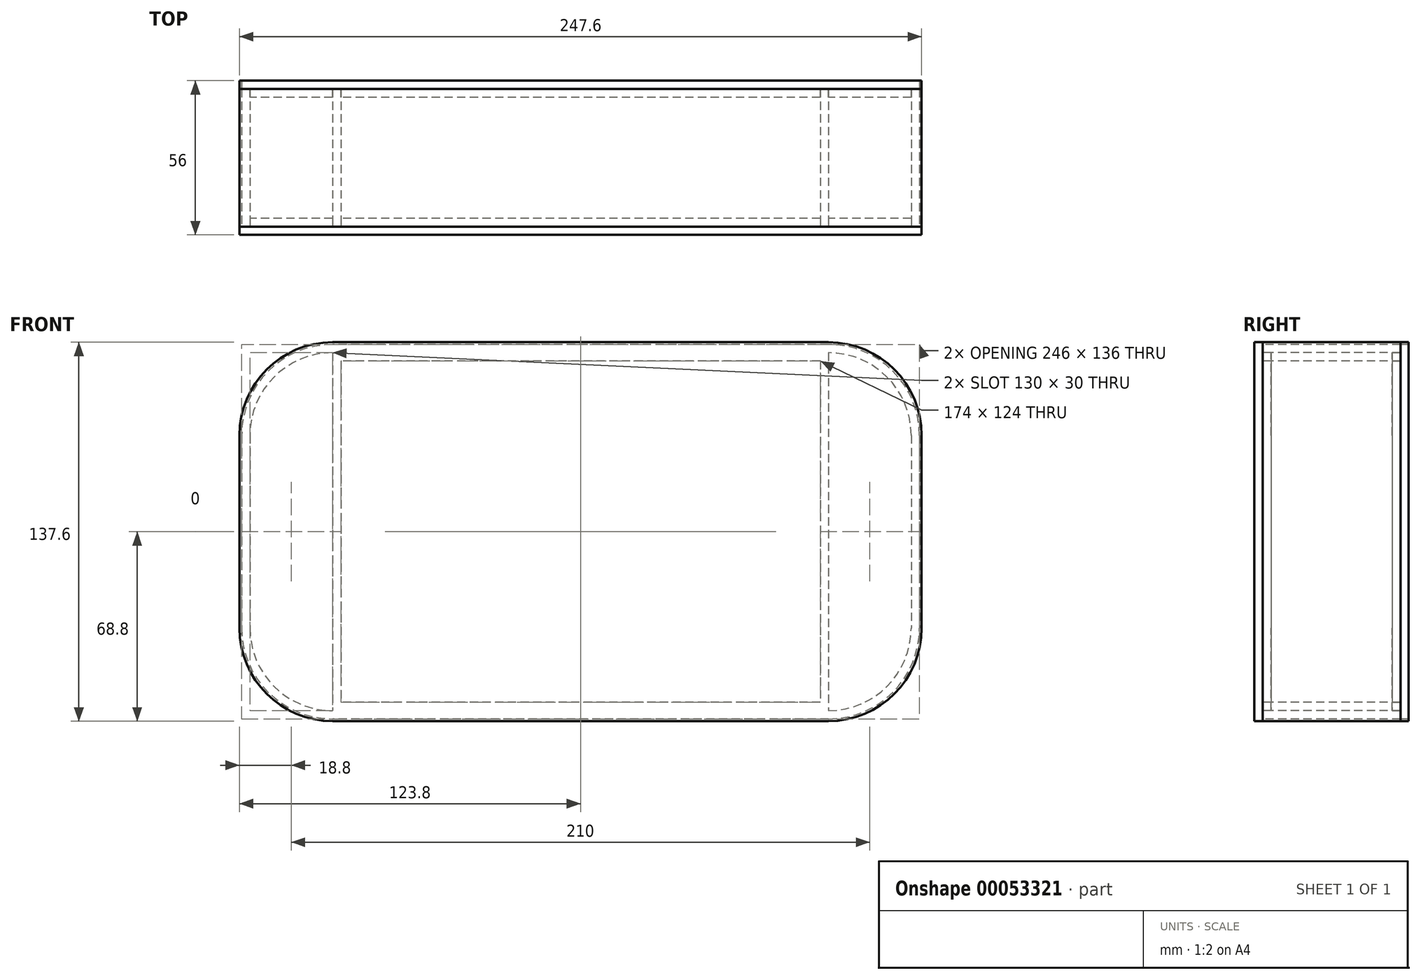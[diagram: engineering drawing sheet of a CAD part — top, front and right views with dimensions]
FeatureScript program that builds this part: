
annotation { "Feature Type Name" : "Feature", "Feature Type Description" : "" }
export const myFeature = defineFeature(function(context is Context, id is Id, definition is map)
    precondition{}
    {
        {
            var Q0;
            Q0=qCreatedBy(makeId("Front.planeOp"),FACE);
            var sketch = newSketch(context, id + "F0", { "sketchPlane" : qUnion([Q0])});
            skLineSegment(sketch, "E0.rect.bottom", {"start": v(90, 65) * mm, "end": v(-90, 65) * mm});
            skLineSegment(sketch, "E0.rect.top", {"start": v(90, -65) * mm, "end": v(-90, -65) * mm});
            skLineSegment(sketch, "E0.rect.left", {"start": v(120, 35) * mm, "end": v(120, -35) * mm});
            skLineSegment(sketch, "E0.rect.right", {"start": v(-120, 35) * mm, "end": v(-120, -35) * mm});
            skPoint(sketch, "E0.rect.middle", {"position": v(0, 0) * mm});
            skPoint(sketch, "E1.visualSharp", {"position": v(-120, 65) * mm});
            skArc(sketch, "E1.filletArc", {"start": v(-90, 65) * mm, "mid": v(-111.21, 56.21) * mm, "end": v(-120, 35) * mm});
            skPoint(sketch, "E2.visualSharp", {"position": v(120, 65) * mm});
            skArc(sketch, "E2.filletArc", {"start": v(120, 35) * mm, "mid": v(111.21, 56.21) * mm, "end": v(90, 65) * mm});
            skPoint(sketch, "E3.visualSharp", {"position": v(120, -65) * mm});
            skArc(sketch, "E3.filletArc", {"start": v(90, -65) * mm, "mid": v(111.21, -56.21) * mm, "end": v(120, -35) * mm});
            skPoint(sketch, "E4.visualSharp", {"position": v(-120, -65) * mm});
            skArc(sketch, "E4.filletArc", {"start": v(-120, -35) * mm, "mid": v(-111.21, -56.21) * mm, "end": v(-90, -65) * mm});
            skLineSegment(sketch, "E5.0", {"start": v(-123, 35) * mm, "end": v(-123, -35) * mm});
            skArc(sketch, "E5.1", {"start": v(-90, 68) * mm, "mid": v(-113.33, 58.33) * mm, "end": v(-123, 35) * mm});
            skLineSegment(sketch, "E5.2", {"start": v(90, 68) * mm, "end": v(-90, 68) * mm});
            skArc(sketch, "E6.0", {"start": v(123, 35) * mm, "mid": v(113.33, 58.33) * mm, "end": v(90, 68) * mm});
            skArc(sketch, "E6.1", {"start": v(-123, -35) * mm, "mid": v(-113.33, -58.33) * mm, "end": v(-90, -68) * mm});
            skLineSegment(sketch, "E6.2", {"start": v(90, -68) * mm, "end": v(-90, -68) * mm});
            skArc(sketch, "E6.3", {"start": v(90, -68) * mm, "mid": v(113.33, -58.33) * mm, "end": v(123, -35) * mm});
            skLineSegment(sketch, "E6.4", {"start": v(123, 35) * mm, "end": v(123, -35) * mm});
            skLineSegment(sketch, "E7.0", {"start": v(90, 68.8) * mm, "end": v(-90, 68.8) * mm});
            skArc(sketch, "E7.1", {"start": v(123.8, 35) * mm, "mid": v(113.9, 58.9) * mm, "end": v(90, 68.8) * mm});
            skArc(sketch, "E7.2", {"start": v(-90, 68.8) * mm, "mid": v(-113.9, 58.9) * mm, "end": v(-123.8, 35) * mm});
            skLineSegment(sketch, "E7.3", {"start": v(123.8, 35) * mm, "end": v(123.8, -35) * mm});
            skLineSegment(sketch, "E7.4", {"start": v(-123.8, 35) * mm, "end": v(-123.8, -35) * mm});
            skArc(sketch, "E7.5", {"start": v(-123.8, -35) * mm, "mid": v(-113.9, -58.9) * mm, "end": v(-90, -68.8) * mm});
            skLineSegment(sketch, "E7.6", {"start": v(90, -68.8) * mm, "end": v(-90, -68.8) * mm});
            skArc(sketch, "E7.7", {"start": v(90, -68.8) * mm, "mid": v(113.9, -58.9) * mm, "end": v(123.8, -35) * mm});
            skLineSegment(sketch, "E8.left", {"start": v(90, 65) * mm, "end": v(90, -65) * mm});
            skLineSegment(sketch, "E8.right", {"start": v(-90, 65) * mm, "end": v(-90, -65) * mm});
            skLineSegment(sketch, "E9.0", {"start": v(87, 62) * mm, "end": v(-87, 62) * mm});
            skLineSegment(sketch, "E9.1", {"start": v(87, 62) * mm, "end": v(87, -62) * mm});
            skLineSegment(sketch, "E9.2", {"start": v(87, -62) * mm, "end": v(-87, -62) * mm});
            skLineSegment(sketch, "E9.3", {"start": v(-87, 62) * mm, "end": v(-87, -62) * mm});
            skSolve(sketch);
        }
        {
            var Q0;
            Q0=makeQuery(id+"F0.imprint","IMPRINT",FACE,{"disambiguationData":[TD([[makeQuery(id+"F0.imprint","IMPRINT",EDGE,{"derivedFrom":sQuery(id+"F0.wireOp",EDGE,"E0.rect.bottom")}),1.0]])]});
            var Q1;
            Q1=makeQuery(id+"F0.imprint","IMPRINT",FACE,{"disambiguationData":[TD([[makeQuery(id+"F0.imprint","IMPRINT",EDGE,{"derivedFrom":sQuery(id+"F0.wireOp",EDGE,"E0.rect.left")}),1.0]])]});
            extrude(context, id + "F1", {"entities" : qUnion([Q0, Q1]), "oppositeDirection" : true, "depth" : 50 * mm});
        }
        {
            var Q0;
            Q0=makeQuery(id+"F0.imprint","IMPRINT",FACE,{"disambiguationData":[TD([[makeQuery(id+"F0.imprint","IMPRINT",EDGE,{"derivedFrom":sQuery(id+"F0.wireOp",EDGE,"E9.0")}),1.0]])]});
            var Q1;
            Q1=makeQuery(id+"F0.imprint","IMPRINT",FACE,{"disambiguationData":[TD([[makeQuery(id+"F0.imprint","IMPRINT",EDGE,{"derivedFrom":sQuery(id+"F0.wireOp",EDGE,"E0.rect.right")}),1.0]])]});
            var Q2;
            Q2=makeQuery(id+"F0.imprint","IMPRINT",FACE,{"disambiguationData":[TD([[makeQuery(id+"F0.imprint","IMPRINT",EDGE,{"derivedFrom":sQuery(id+"F0.wireOp",EDGE,"E0.rect.left")}),-1.0]])]});
            extrude(context, id + "F2", {"entities" : qUnion([Q0, Q1, Q2]), "oppositeDirection" : true, "depth" : 3 * mm});
        }
        {
            var Q0;
            Q0=makeQuery(id+"F0.imprint","IMPRINT",FACE,{"disambiguationData":[TD([[makeQuery(id+"F0.imprint","IMPRINT",EDGE,{"derivedFrom":sQuery(id+"F0.wireOp",EDGE,"E5.0")}),-1.0]])]});
            var Q1;
            Q1=makeQuery(id+"F0.imprint","IMPRINT",FACE,{"disambiguationData":[TD([[makeQuery(id+"F0.imprint","IMPRINT",EDGE,{"derivedFrom":sQuery(id+"F0.wireOp",EDGE,"E0.rect.left")}),1.0]])]});
            var Q2;
            Q2=makeQuery(id+"F0.imprint","IMPRINT",FACE,{"disambiguationData":[TD([[makeQuery(id+"F0.imprint","IMPRINT",EDGE,{"derivedFrom":sQuery(id+"F0.wireOp",EDGE,"E0.rect.bottom")}),1.0]])]});
            var Q3;
            Q3=makeQuery(id+"F0.imprint","IMPRINT",FACE,{"disambiguationData":[TD([[makeQuery(id+"F0.imprint","IMPRINT",EDGE,{"derivedFrom":sQuery(id+"F0.wireOp",EDGE,"E9.0")}),1.0]])]});
            var Q4;
            Q4=makeQuery(id+"F0.imprint","IMPRINT",FACE,{"disambiguationData":[TD([[makeQuery(id+"F0.imprint","IMPRINT",EDGE,{"derivedFrom":sQuery(id+"F0.wireOp",EDGE,"E0.rect.right")}),1.0]])]});
            var Q5;
            Q5=makeQuery(id+"F0.imprint","IMPRINT",FACE,{"disambiguationData":[TD([[makeQuery(id+"F0.imprint","IMPRINT",EDGE,{"derivedFrom":sQuery(id+"F0.wireOp",EDGE,"E0.rect.left")}),-1.0]])]});
            extrude(context, id + "F3", {"entities" : qUnion([Q0, Q1, Q2, Q3, Q4, Q5]), "depth" : 3 * mm});
        }
        {
            var Q0;
            Q0=makeQuery(id+"F0.imprint","IMPRINT",FACE,{"disambiguationData":[TD([[makeQuery(id+"F0.imprint","IMPRINT",EDGE,{"derivedFrom":sQuery(id+"F0.wireOp",EDGE,"E5.0")}),-1.0]])]});
            extrude(context, id + "F4", {"entities" : qUnion([Q0]), "oppositeDirection" : true, "depth" : 50 * mm});
        }
        {
            var Q0;
            Q0=makeQuery(id+"F1.opExtrude","CAP_FACE",FACE,{"disambiguationData":[OSD([sQuery(id+"F0.wireOp",EDGE,"E0.rect.left"),sQuery(id+"F0.wireOp",EDGE,"E0.rect.right"),sQuery(id+"F0.wireOp",EDGE,"E1.filletArc"),sQuery(id+"F0.wireOp",EDGE,"E2.filletArc"),sQuery(id+"F0.wireOp",EDGE,"E3.filletArc"),sQuery(id+"F0.wireOp",EDGE,"E4.filletArc"),sQuery(id+"F0.wireOp",EDGE,"E5.0"),sQuery(id+"F0.wireOp",EDGE,"E5.1"),sQuery(id+"F0.wireOp",EDGE,"E5.2"),sQuery(id+"F0.wireOp",EDGE,"E6.0"),sQuery(id+"F0.wireOp",EDGE,"E6.1"),sQuery(id+"F0.wireOp",EDGE,"E6.2"),sQuery(id+"F0.wireOp",EDGE,"E6.3"),sQuery(id+"F0.wireOp",EDGE,"E6.4"),sQuery(id+"F0.wireOp",EDGE,"E8.left"),sQuery(id+"F0.wireOp",EDGE,"E8.right"),sQuery(id+"F0.wireOp",EDGE,"E9.0"),sQuery(id+"F0.wireOp",EDGE,"E9.1"),sQuery(id+"F0.wireOp",EDGE,"E9.2"),sQuery(id+"F0.wireOp",EDGE,"E9.3")])],"isStart":false});
            var sketch = newSketch(context, id + "F5", { "sketchPlane" : qUnion([Q0])});
            skArc(sketch, "E10.0", {"start": v(-120, 35) * mm, "mid": v(-111.21, 56.21) * mm, "end": v(-90, 65) * mm});
            skLineSegment(sketch, "E11.0", {"start": v(-120, 35) * mm, "end": v(-120, -35) * mm});
            skArc(sketch, "E12.0", {"start": v(-90, -65) * mm, "mid": v(-111.21, -56.21) * mm, "end": v(-120, -35) * mm});
            skLineSegment(sketch, "E13.0", {"start": v(-90, 65) * mm, "end": v(-90, -65) * mm});
            skLineSegment(sketch, "E14.0", {"start": v(90, 65) * mm, "end": v(90, -65) * mm});
            skArc(sketch, "E15.0", {"start": v(90, 65) * mm, "mid": v(111.21, 56.21) * mm, "end": v(120, 35) * mm});
            skLineSegment(sketch, "E16.0", {"start": v(120, 35) * mm, "end": v(120, -35) * mm});
            skArc(sketch, "E17.0", {"start": v(120, -35) * mm, "mid": v(111.21, -56.21) * mm, "end": v(90, -65) * mm});
            skSolve(sketch);
        }
        {
            var Q0;
            Q0=makeQuery(id+"F5.imprint","IMPRINT",FACE,{"disambiguationData":[TD([[makeQuery(id+"F5.imprint","IMPRINT",EDGE,{"derivedFrom":makeQuery(id+"F1.opExtrude","CAP_EDGE",EDGE,{"disambiguationData":[OSD([sQuery(id+"F0.wireOp",EDGE,"E9.0")])],"isStart":false})}),-1.0]])]});
            var Q1;
            Q1=makeQuery(id+"F5.imprint","IMPRINT",FACE,{"disambiguationData":[TD([[makeQuery(id+"F5.imprint","IMPRINT",EDGE,{"derivedFrom":sQuery(id+"F5.wireOp",EDGE,"E14.0")}),1.0]])]});
            var Q2;
            Q2=makeQuery(id+"F5.imprint","IMPRINT",FACE,{"disambiguationData":[TD([[makeQuery(id+"F5.imprint","IMPRINT",EDGE,{"derivedFrom":sQuery(id+"F5.wireOp",EDGE,"E10.0")}),-1.0]])]});
            extrude(context, id + "F6", {"entities" : qUnion([Q0, Q1, Q2]), "oppositeDirection" : true, "depth" : 3 * mm});
        }
        {
            var Q0;
            Q0=makeQuery(id+"F5.imprint","IMPRINT",FACE,{"disambiguationData":[TD([[makeQuery(id+"F5.imprint","IMPRINT",EDGE,{"derivedFrom":sQuery(id+"F5.wireOp",EDGE,"E10.0")}),-1.0]])]});
            var Q1;
            Q1=makeQuery(id+"F5.imprint","IMPRINT",FACE,{"disambiguationData":[TD([[makeQuery(id+"F5.imprint","IMPRINT",EDGE,{"derivedFrom":sQuery(id+"F5.wireOp",EDGE,"E10.0")}),1.0]])]});
            var Q2;
            Q2=makeQuery(id+"F5.imprint","IMPRINT",FACE,{"disambiguationData":[TD([[makeQuery(id+"F5.imprint","IMPRINT",EDGE,{"derivedFrom":makeQuery(id+"F1.opExtrude","CAP_EDGE",EDGE,{"disambiguationData":[OSD([sQuery(id+"F0.wireOp",EDGE,"E9.0")])],"isStart":false})}),-1.0]])]});
            var Q3;
            Q3=makeQuery(id+"F4.opExtrude","CAP_FACE",FACE,{"disambiguationData":[OSD([sQuery(id+"F0.wireOp",EDGE,"E5.0"),sQuery(id+"F0.wireOp",EDGE,"E5.1"),sQuery(id+"F0.wireOp",EDGE,"E5.2"),sQuery(id+"F0.wireOp",EDGE,"E6.0"),sQuery(id+"F0.wireOp",EDGE,"E6.1"),sQuery(id+"F0.wireOp",EDGE,"E6.2"),sQuery(id+"F0.wireOp",EDGE,"E6.3"),sQuery(id+"F0.wireOp",EDGE,"E6.4"),sQuery(id+"F0.wireOp",EDGE,"E7.0"),sQuery(id+"F0.wireOp",EDGE,"E7.1"),sQuery(id+"F0.wireOp",EDGE,"E7.2"),sQuery(id+"F0.wireOp",EDGE,"E7.3"),sQuery(id+"F0.wireOp",EDGE,"E7.4"),sQuery(id+"F0.wireOp",EDGE,"E7.5"),sQuery(id+"F0.wireOp",EDGE,"E7.6"),sQuery(id+"F0.wireOp",EDGE,"E7.7")])],"isStart":false});
            var Q4;
            Q4=makeQuery(id+"F5.imprint","IMPRINT",FACE,{"disambiguationData":[TD([[makeQuery(id+"F5.imprint","IMPRINT",EDGE,{"derivedFrom":sQuery(id+"F5.wireOp",EDGE,"E14.0")}),1.0]])]});
            extrude(context, id + "F7", {"entities" : qUnion([Q0, Q1, Q2, Q3, Q4]), "depth" : 3 * mm});
        }
    });
